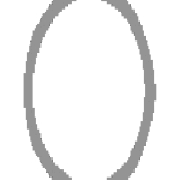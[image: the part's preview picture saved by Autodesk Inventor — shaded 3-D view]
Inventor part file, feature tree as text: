
AUTODESK INVENTOR PART (.ipt)
format: ipt  version: 2021 (Build 250183000, 183)  size: 110,080 bytes
history: native  units: in
note: dims shown in document units (in); Inventor stores cm internally (conversion verified against a paired STEP export)
features: other x4, sketch x3, plane x1
ambient origin geometry x8: Origin, YZ Plane, XZ Plane, XY Plane, X Axis, Y Axis, Z Axis, Center Point
bodies: Solid1 (feature_tree), Body (feature_tree)
feature tree (8):
  other  "Driven Length"
  other  "Frame Generator"
  other  "Start Plane"
  other  "End Plane"
  sketch  "Sketch"  dims[d2=13.0in d4=-0.0in d5=13.0in d6=0.12in d7=0.0in d10=90.0deg d9=13.0in]
  sketch  "Sketch4"  dims[d0=1.0in]
  plane  "Work Plane4"
  sketch  "Sketch5"  dims[d1=0.065in]
